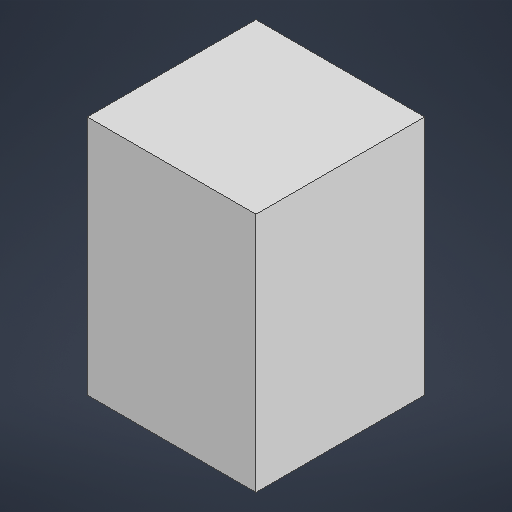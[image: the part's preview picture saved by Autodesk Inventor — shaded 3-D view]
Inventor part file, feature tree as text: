
AUTODESK INVENTOR PART (.ipt)
format: ipt  version: 2025.2 (Build 292293000, 293)  size: 392,704 bytes
history: native  units: mm
features: extrude x1, sketch x1
ambient origin geometry x8: Origin, YZ Plane, XZ Plane, XY Plane, X Axis, Y Axis, Z Axis, Center Point
bodies: Solid1 (feature_tree)
feature tree (2):
  extrude  "Extrusion1"  Depth=14.0mm
  sketch  "Sketch1"  dims[d0=14.0mm d1=14.0mm d2=20.0mm d3=0.0mm]
